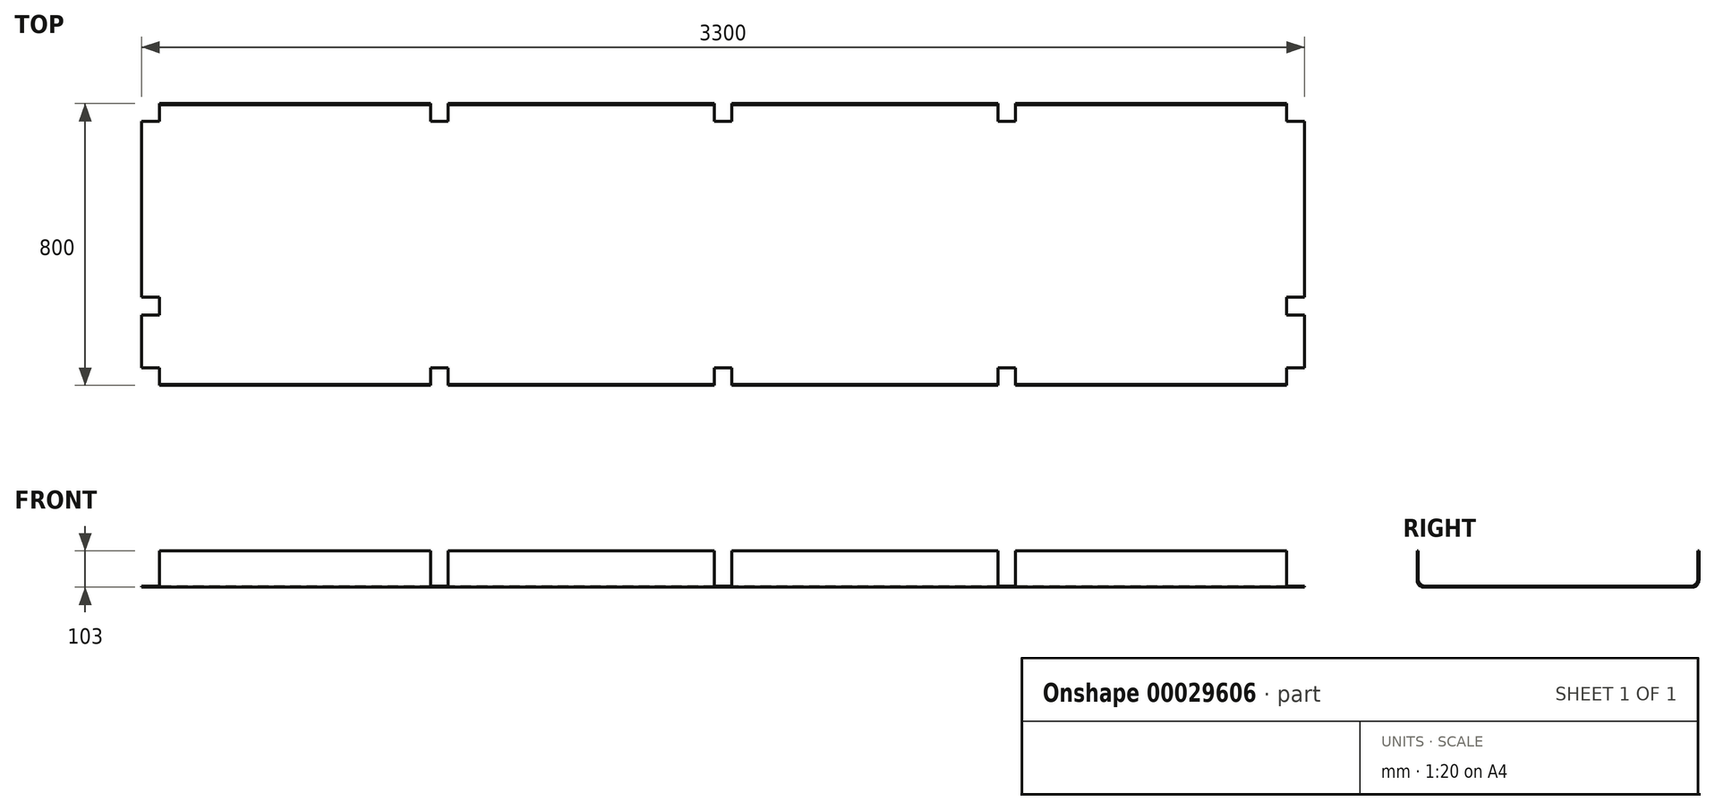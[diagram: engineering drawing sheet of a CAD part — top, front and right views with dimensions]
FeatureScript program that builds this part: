
annotation { "Feature Type Name" : "Feature", "Feature Type Description" : "" }
export const myFeature = defineFeature(function(context is Context, id is Id, definition is map)
    precondition{}
    {
        {
            var Q0;
            Q0=qCreatedBy(makeId("Right.planeOp"),FACE);
            var sketch = newSketch(context, id + "F0", { "sketchPlane" : qUnion([Q0])});
            skLineSegment(sketch, "E0.rect.bottom", {"start": v(-377, 1.5) * mm, "end": v(377, 1.5) * mm});
            skLineSegment(sketch, "E0.rect.top", {"start": v(-380, -1.5) * mm, "end": v(380, -1.5) * mm});
            skPoint(sketch, "E0.rect.middle", {"position": v(0, 0) * mm});
            skLineSegment(sketch, "E1.top", {"start": v(-400, 101.5) * mm, "end": v(-397, 101.5) * mm});
            skLineSegment(sketch, "E1.left", {"start": v(-400, 18.5) * mm, "end": v(-400, 101.5) * mm});
            skLineSegment(sketch, "E1.right", {"start": v(-397, 21.5) * mm, "end": v(-397, 101.5) * mm});
            skLineSegment(sketch, "E2.MirrorCS", {"start": v(400, 18.5) * mm, "end": v(400, 101.5) * mm});
            skLineSegment(sketch, "E3.MirrorCS", {"start": v(397, 21.5) * mm, "end": v(397, 101.5) * mm});
            skLineSegment(sketch, "E4.MirrorCS", {"start": v(400, 101.5) * mm, "end": v(397, 101.5) * mm});
            skArc(sketch, "E5.filletArc", {"start": v(-397, 21.5) * mm, "mid": v(-391.14, 7.36) * mm, "end": v(-377, 1.5) * mm});
            skArc(sketch, "E6.filletArc", {"start": v(-400, 18.5) * mm, "mid": v(-394.14, 4.36) * mm, "end": v(-380, -1.5) * mm});
            skArc(sketch, "E7.filletArc", {"start": v(380, -1.5) * mm, "mid": v(394.14, 4.36) * mm, "end": v(400, 18.5) * mm});
            skArc(sketch, "E8.filletArc", {"start": v(377, 1.5) * mm, "mid": v(391.14, 7.36) * mm, "end": v(397, 21.5) * mm});
            skSolve(sketch);
        }
        {
            var Q0;
            Q0=makeQuery(id+"F0.imprint","IMPRINT",FACE,{"disambiguationData":[TD([[makeQuery(id+"F0.imprint","IMPRINT",EDGE,{"derivedFrom":sQuery(id+"F0.wireOp",EDGE,"E0.rect.bottom")}),-1.0]])]});
            extrude(context, id + "F1", {"entities" : qUnion([Q0]), "endBound" : BoundingType.SYMMETRIC, "depth" : 3300 * mm});
        }
        {
            var Q0;
            Q0=qCreatedBy(makeId("Top.planeOp"),FACE);
            var sketch = newSketch(context, id + "F2", { "sketchPlane" : qUnion([Q0])});
            skLineSegment(sketch, "E9", {"start": v(0, 0) * mm, "end": v(0, 410.4) * mm});
            skLineSegment(sketch, "E10", {"start": v(0, 0) * mm, "end": v(1610, 0) * mm});
            skLineSegment(sketch, "E11.rect.bottom", {"start": v(25, 400) * mm, "end": v(-25, 400) * mm});
            skLineSegment(sketch, "E11.rect.top", {"start": v(25, 350) * mm, "end": v(-25, 350) * mm});
            skLineSegment(sketch, "E11.rect.left", {"start": v(25, 400) * mm, "end": v(25, 350) * mm});
            skLineSegment(sketch, "E11.rect.right", {"start": v(-25, 400) * mm, "end": v(-25, 350) * mm});
            skPoint(sketch, "E11.rect.middle", {"position": v(0, 375) * mm});
            skLineSegment(sketch, "E12.rect.bottom", {"start": v(1650, 400) * mm, "end": v(1600, 400) * mm});
            skLineSegment(sketch, "E12.rect.top", {"start": v(1650, 350) * mm, "end": v(1600, 350) * mm});
            skLineSegment(sketch, "E12.rect.left", {"start": v(1650, 400) * mm, "end": v(1650, 350) * mm});
            skLineSegment(sketch, "E12.rect.right", {"start": v(1600, 400) * mm, "end": v(1600, 350) * mm});
            skPoint(sketch, "E12.rect.middle", {"position": v(1625, 375) * mm});
            skLineSegment(sketch, "E13.rect.bottom", {"start": v(830, 400) * mm, "end": v(780, 400) * mm});
            skLineSegment(sketch, "E13.rect.top", {"start": v(830, 350) * mm, "end": v(780, 350) * mm});
            skLineSegment(sketch, "E13.rect.left", {"start": v(830, 400) * mm, "end": v(830, 350) * mm});
            skLineSegment(sketch, "E13.rect.right", {"start": v(780, 400) * mm, "end": v(780, 350) * mm});
            skPoint(sketch, "E13.rect.middle", {"position": v(805, 375) * mm});
            skLineSegment(sketch, "E14", {"start": v(805, 0) * mm, "end": v(805, 443.54) * mm});
            skLineSegment(sketch, "E15.MirrorCS", {"start": v(-830, 400) * mm, "end": v(-780, 400) * mm});
            skLineSegment(sketch, "E16.MirrorCS", {"start": v(-780, 400) * mm, "end": v(-780, 350) * mm});
            skLineSegment(sketch, "E17.MirrorCS", {"start": v(-830, 350) * mm, "end": v(-780, 350) * mm});
            skLineSegment(sketch, "E18.MirrorCS", {"start": v(-830, 400) * mm, "end": v(-830, 350) * mm});
            skPoint(sketch, "E19.MirrorP", {"position": v(-805, 375) * mm});
            skLineSegment(sketch, "E20.MirrorCS", {"start": v(-1650, 400) * mm, "end": v(-1600, 400) * mm});
            skLineSegment(sketch, "E21.MirrorCS", {"start": v(-1650, 400) * mm, "end": v(-1650, 350) * mm});
            skLineSegment(sketch, "E22.MirrorCS", {"start": v(-1600, 400) * mm, "end": v(-1600, 350) * mm});
            skLineSegment(sketch, "E23.MirrorCS", {"start": v(-1650, 350) * mm, "end": v(-1600, 350) * mm});
            skPoint(sketch, "E24.MirrorP", {"position": v(-1625, 375) * mm});
            skLineSegment(sketch, "E25.MirrorCS", {"start": v(830, -400) * mm, "end": v(780, -400) * mm});
            skLineSegment(sketch, "E26.MirrorCS", {"start": v(1650, -400) * mm, "end": v(1600, -400) * mm});
            skLineSegment(sketch, "E27.MirrorCS", {"start": v(-25, -400) * mm, "end": v(-25, -350) * mm});
            skLineSegment(sketch, "E28.MirrorCS", {"start": v(25, -400) * mm, "end": v(25, -350) * mm});
            skLineSegment(sketch, "E29.MirrorCS", {"start": v(25, -350) * mm, "end": v(-25, -350) * mm});
            skLineSegment(sketch, "E30.MirrorCS", {"start": v(25, -400) * mm, "end": v(-25, -400) * mm});
            skLineSegment(sketch, "E31.MirrorCS", {"start": v(1650, -350) * mm, "end": v(1600, -350) * mm});
            skLineSegment(sketch, "E32.MirrorCS", {"start": v(1650, -400) * mm, "end": v(1650, -350) * mm});
            skLineSegment(sketch, "E33.MirrorCS", {"start": v(1600, -400) * mm, "end": v(1600, -350) * mm});
            skLineSegment(sketch, "E34.MirrorCS", {"start": v(830, -350) * mm, "end": v(780, -350) * mm});
            skLineSegment(sketch, "E35.MirrorCS", {"start": v(780, -400) * mm, "end": v(780, -350) * mm});
            skLineSegment(sketch, "E36.MirrorCS", {"start": v(-830, -400) * mm, "end": v(-780, -400) * mm});
            skLineSegment(sketch, "E37.MirrorCS", {"start": v(830, -400) * mm, "end": v(830, -350) * mm});
            skLineSegment(sketch, "E38.MirrorCS", {"start": v(-1650, -350) * mm, "end": v(-1600, -350) * mm});
            skLineSegment(sketch, "E39.MirrorCS", {"start": v(-1650, -400) * mm, "end": v(-1650, -350) * mm});
            skLineSegment(sketch, "E40.MirrorCS", {"start": v(-830, -350) * mm, "end": v(-780, -350) * mm});
            skLineSegment(sketch, "E41.MirrorCS", {"start": v(-1650, -400) * mm, "end": v(-1600, -400) * mm});
            skLineSegment(sketch, "E42.MirrorCS", {"start": v(-830, -400) * mm, "end": v(-830, -350) * mm});
            skLineSegment(sketch, "E43.MirrorCS", {"start": v(-780, -400) * mm, "end": v(-780, -350) * mm});
            skLineSegment(sketch, "E44.MirrorCS", {"start": v(-1600, -400) * mm, "end": v(-1600, -350) * mm});
            skPoint(sketch, "E45.MirrorP", {"position": v(-1625, -375) * mm});
            skPoint(sketch, "E46.MirrorP", {"position": v(805, -375) * mm});
            skPoint(sketch, "E47.MirrorP", {"position": v(1625, -375) * mm});
            skPoint(sketch, "E48.MirrorP", {"position": v(0, -375) * mm});
            skPoint(sketch, "E49.MirrorP", {"position": v(-805, -375) * mm});
            skLineSegment(sketch, "E50.bottom", {"start": v(-1650, -100) * mm, "end": v(-1600, -100) * mm});
            skLineSegment(sketch, "E50.top", {"start": v(-1650, -150) * mm, "end": v(-1600, -150) * mm});
            skLineSegment(sketch, "E50.left", {"start": v(-1650, -100) * mm, "end": v(-1650, -150) * mm});
            skLineSegment(sketch, "E50.right", {"start": v(-1600, -100) * mm, "end": v(-1600, -150) * mm});
            skSolve(sketch);
        }
        {
            var Q0;
            Q0=makeQuery(id+"F2.imprint","IMPRINT",FACE,{"disambiguationData":[TD([[makeQuery(id+"F2.imprint","IMPRINT",EDGE,{"derivedFrom":sQuery(id+"F2.wireOp",EDGE,"E15.MirrorCS")}),-1.0]])]});
            var Q1;
            Q1=makeQuery(id+"F2.imprint","IMPRINT",FACE,{"disambiguationData":[TD([[makeQuery(id+"F2.imprint","IMPRINT",EDGE,{"derivedFrom":sQuery(id+"F2.wireOp",EDGE,"E20.MirrorCS")}),-1.0]])]});
            var Q2;
            Q2=makeQuery(id+"F2.imprint","IMPRINT",FACE,{"disambiguationData":[TD([[makeQuery(id+"F2.imprint","IMPRINT",EDGE,{"derivedFrom":sQuery(id+"F2.wireOp",EDGE,"E26.MirrorCS")}),-1.0]])]});
            var Q3;
            Q3=makeQuery(id+"F2.imprint","IMPRINT",FACE,{"disambiguationData":[TD([[makeQuery(id+"F2.imprint","IMPRINT",EDGE,{"derivedFrom":sQuery(id+"F2.wireOp",EDGE,"E36.MirrorCS")}),1.0]])]});
            var Q4;
            Q4=makeQuery(id+"F2.imprint","IMPRINT",FACE,{"disambiguationData":[TD([[makeQuery(id+"F2.imprint","IMPRINT",EDGE,{"derivedFrom":sQuery(id+"F2.wireOp",EDGE,"E38.MirrorCS")}),-1.0]])]});
            var Q5;
            Q5=makeQuery(id+"F2.imprint","IMPRINT",FACE,{"disambiguationData":[TD([[makeQuery(id+"F2.imprint","IMPRINT",EDGE,{"derivedFrom":sQuery(id+"F2.wireOp",EDGE,"E27.MirrorCS")}),-1.0]])]});
            var Q6;
            Q6=makeQuery(id+"F2.imprint","IMPRINT",FACE,{"disambiguationData":[TD([[makeQuery(id+"F2.imprint","IMPRINT",EDGE,{"derivedFrom":sQuery(id+"F2.wireOp",EDGE,"E25.MirrorCS")}),-1.0]])]});
            var Q7;
            Q7=makeQuery(id+"F2.imprint","IMPRINT",FACE,{"disambiguationData":[TD([[makeQuery(id+"F2.imprint","IMPRINT",EDGE,{"derivedFrom":sQuery(id+"F2.wireOp",EDGE,"E12.rect.bottom")}),1.0]])]});
            var Q8;
            {var subQ5=sQuery(id+"F2.wireOp",EDGE,"E13.rect.right");Q8=makeQuery(id+"F2.imprint","IMPRINT",FACE,{"disambiguationData":[TD([[makeQuery(id+"F2.imprint","IMPRINT",EDGE,{"derivedFrom":subQ5}),1.0]])]});}
            var Q9;
            {var subQ5=sQuery(id+"F2.wireOp",EDGE,"E13.rect.left");Q9=makeQuery(id+"F2.imprint","IMPRINT",FACE,{"disambiguationData":[TD([[makeQuery(id+"F2.imprint","IMPRINT",EDGE,{"derivedFrom":subQ5}),-1.0]])]});}
            var Q10;
            {var subQ0=sQuery(id+"F2.wireOp",EDGE,"E11.rect.right");Q10=makeQuery(id+"F2.imprint","IMPRINT",FACE,{"disambiguationData":[TD([[makeQuery(id+"F2.imprint","IMPRINT",EDGE,{"derivedFrom":subQ0}),1.0]])]});}
            var Q11;
            {var subQ0=sQuery(id+"F2.wireOp",EDGE,"E11.rect.left");Q11=makeQuery(id+"F2.imprint","IMPRINT",FACE,{"disambiguationData":[TD([[makeQuery(id+"F2.imprint","IMPRINT",EDGE,{"derivedFrom":subQ0}),-1.0]])]});}
            extrude(context, id + "F3", {"entities" : qUnion([Q0, Q1, Q2, Q3, Q4, Q5, Q6, Q7, Q8, Q9, Q10, Q11]), "operationType" : NewBodyOperationType.REMOVE, "endBound" : BoundingType.THROUGH_ALL, "depth" : 25 * mm, "hasSecondDirection" : true, "secondDirectionBound" : SecondDirectionBoundingType.THROUGH_ALL, "secondDirectionOppositeDirection" : true, "secondDirectionDepth" : 25 * mm});
        }
        {
            var Q0;
            Q0=makeQuery(id+"F1.opExtrude","SWEPT_FACE",FACE,{"disambiguationData":[OSD([sQuery(id+"F0.wireOp",EDGE,"E0.rect.bottom")])]});
            var sketch = newSketch(context, id + "F4", { "sketchPlane" : qUnion([Q0])});
            skLineSegment(sketch, "E51.bottom", {"start": v(-1650, -150) * mm, "end": v(-1600, -150) * mm});
            skLineSegment(sketch, "E51.top", {"start": v(-1650, -200) * mm, "end": v(-1600, -200) * mm});
            skLineSegment(sketch, "E51.left", {"start": v(-1650, -150) * mm, "end": v(-1650, -200) * mm});
            skLineSegment(sketch, "E51.right", {"start": v(-1600, -150) * mm, "end": v(-1600, -200) * mm});
            skLineSegment(sketch, "E52.bottom", {"start": v(1650, -200) * mm, "end": v(1600, -200) * mm});
            skLineSegment(sketch, "E52.top", {"start": v(1650, -150) * mm, "end": v(1600, -150) * mm});
            skLineSegment(sketch, "E52.left", {"start": v(1650, -200) * mm, "end": v(1650, -150) * mm});
            skLineSegment(sketch, "E52.right", {"start": v(1600, -200) * mm, "end": v(1600, -150) * mm});
            skSolve(sketch);
        }
        {
            var Q0;
            Q0=makeQuery(id+"F4.imprint","IMPRINT",FACE,{"disambiguationData":[TD([[makeQuery(id+"F4.imprint","IMPRINT",EDGE,{"derivedFrom":sQuery(id+"F4.wireOp",EDGE,"E51.bottom")}),-1.0]])]});
            var Q1;
            Q1=makeQuery(id+"F4.imprint","IMPRINT",FACE,{"disambiguationData":[TD([[makeQuery(id+"F4.imprint","IMPRINT",EDGE,{"derivedFrom":sQuery(id+"F4.wireOp",EDGE,"E52.bottom")}),-1.0]])]});
            extrude(context, id + "F5", {"entities" : qUnion([Q0, Q1]), "operationType" : NewBodyOperationType.REMOVE, "endBound" : BoundingType.THROUGH_ALL, "oppositeDirection" : true, "depth" : 25 * mm});
        }
    });
